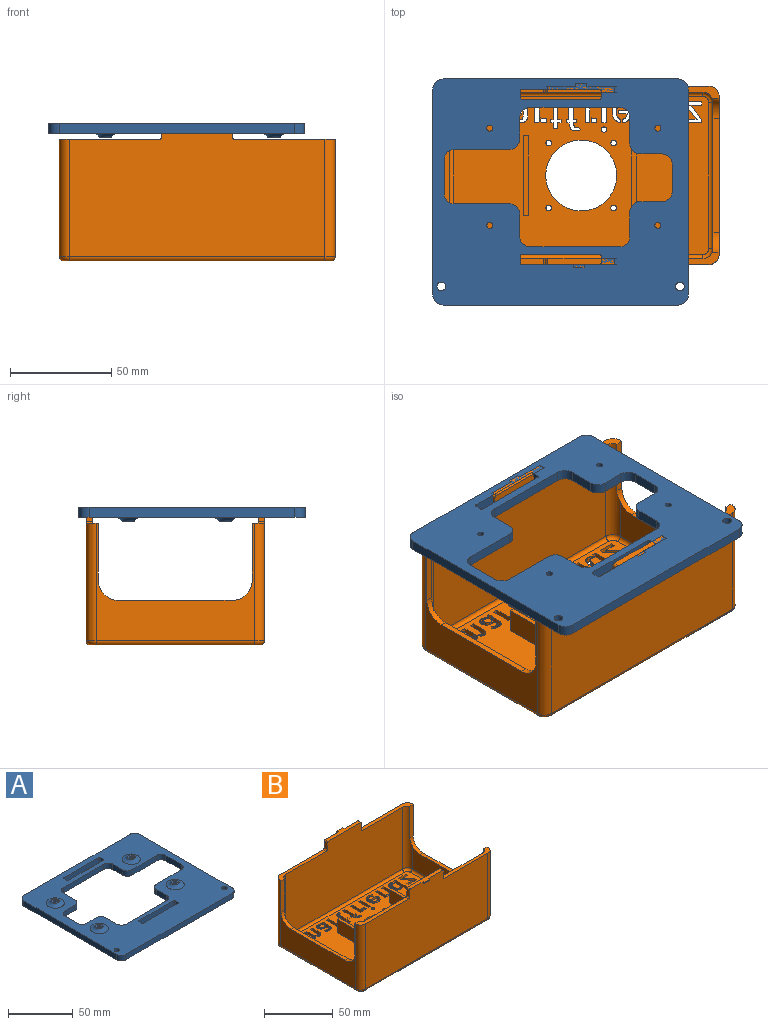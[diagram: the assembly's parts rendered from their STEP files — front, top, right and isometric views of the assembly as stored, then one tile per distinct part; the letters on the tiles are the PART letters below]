
ASSEMBLY  parts=2 mates=1
PART A: 64 faces, bbox 126x111.5x10 mm
  f0: plane 5x3mm, normal (-1,0,0), area 15mm2, adj f18,f19,f22,f27
  f1: plane 38x5mm, normal (0,1,0), area 190mm2, adj f18,f19,f22,f23
  f2: plane 5x3mm, normal (1,0,0), area 15mm2, adj f18,f19,f23,f26
  f3: plane 101.5x5mm, normal (1,0,0), area 507.5mm2, adj f18,f19,f28,f30
  f4: plane 116x5mm, normal (0,1,0), area 580mm2, adj f18,f19,f28,f29
  f5: plane 101.5x5mm, normal (-1,0,0), area 507.5mm2, adj f18,f19,f29,f31
  f6: plane 5x3mm, normal (1,0,0), area 15mm2, adj f18,f19,f20,f25
  f7: plane 38x5mm, normal (0,-1,0), area 190mm2, adj f18,f19,f20,f21
  f8: plane 5x3mm, normal (-1,0,0), area 15mm2, adj f18,f19,f21,f24
  f9: cylinder r=1.5mm len=7mm, axis (0,0,-1), area 66mm2, adj f19,f34
  f10: cylinder r=1.5mm len=7mm, axis (0,0,-1), area 66mm2, adj f19,f33
  f11: cylinder r=1.5mm len=7mm, axis (0,0,-1), area 66mm2, adj f19,f32
  f12: plane 38x5mm, normal (0,-1,0), area 190mm2, adj f18,f19,f26,f27
  f13: cylinder r=2.15mm len=5mm, axis (0,0,-1), area 67.5mm2, adj f18,f19
  f14: cylinder r=2.15mm len=5mm, axis (0,0,-1), area 67.5mm2, adj f18,f19
  f15: plane 116x5mm, normal (0,-1,0), area 580mm2, adj f18,f19,f30,f31
  f16: plane 38x5mm, normal (0,1,0), area 190mm2, adj f18,f19,f24,f25
  f17: cylinder r=1.5mm len=7mm, axis (0,0,-1), area 66mm2, adj f19,f35
  f18: plane 126x111.5mm, normal (0,0,1), area 7777mm2, adj f0,f1,f2,f3,f4,f5,f6,f7
  f19: plane 126x111.5mm, normal (0,0,-1), area 8364.4mm2, adj f0,f1,f2,f3,f4,f5,f6,f7
  f20: cylinder r=1mm len=5mm, axis (0,0,-1), area 7.9mm2, adj f6,f7,f18,f19
  f21: cylinder r=1mm len=5mm, axis (0,0,1), area 7.9mm2, adj f7,f8,f18,f19
  f22: cylinder r=1mm len=5mm, axis (0,0,1), area 7.9mm2, adj f0,f1,f18,f19
  f23: cylinder r=1mm len=5mm, axis (0,0,-1), area 7.9mm2, adj f1,f2,f18,f19
  f24: cylinder r=1mm len=5mm, axis (0,0,-1), area 7.9mm2, adj f8,f16,f18,f19
  f25: cylinder r=1mm len=5mm, axis (0,0,1), area 7.9mm2, adj f6,f16,f18,f19
  f26: cylinder r=1mm len=5mm, axis (0,0,1), area 7.9mm2, adj f2,f12,f18,f19
  f27: cylinder r=1mm len=5mm, axis (0,0,-1), area 7.9mm2, adj f0,f12,f18,f19
  f28: cylinder r=5mm len=5mm, axis (0,0,-1), area 39.3mm2, adj f3,f4,f18,f19
  f29: cylinder r=5mm len=5mm, axis (0,0,1), area 39.3mm2, adj f4,f5,f18,f19
  f30: cylinder r=5mm len=5mm, axis (0,0,1), area 39.3mm2, adj f3,f15,f18,f19
  f31: cylinder r=5mm len=5mm, axis (0,0,-1), area 39.3mm2, adj f5,f15,f18,f19
  f32: plane 6x6mm, normal (0,0,1), area 21.2mm2, adj f11,f39
  f33: plane 6x6mm, normal (0,0,1), area 21.2mm2, adj f10,f38
  f34: plane 6x6mm, normal (0,0,1), area 21.2mm2, adj f9,f37
  f35: plane 6x6mm, normal (0,0,1), area 21.2mm2, adj f17,f36
  f36: torus R=7mm, axis (0,0,1), area 141.1mm2, adj f18,f35
  f37: torus R=7mm, axis (0,0,1), area 141.1mm2, adj f18,f34
  f38: torus R=7mm, axis (0,0,1), area 141.1mm2, adj f18,f33
  f39: torus R=7mm, axis (0,0,1), area 141.1mm2, adj f18,f32
  f40: plane 10.92x5mm, normal (0,1,0), area 54.6mm2, adj f18,f19,f54,f55
  f41: plane 12.23x5mm, normal (1,0,0), area 61.2mm2, adj f18,f19,f55,f62
  f42: plane 44.32x5mm, normal (0,1,0), area 221.6mm2, adj f18,f19,f62,f63
  f43: plane 11.15x5mm, normal (-1,0,0), area 55.7mm2, adj f18,f19,f57,f63
  f44: plane 27.23x5mm, normal (0,1,0), area 136.2mm2, adj f18,f19,f57,f58
  f45: plane 16.9x5mm, normal (-1,0,0), area 84.5mm2, adj f18,f19,f58,f59
  f46: plane 27.23x5mm, normal (0,-1,0), area 136.2mm2, adj f18,f19,f56,f59
  f47: plane 10.72x5mm, normal (-1,0,0), area 53.6mm2, adj f18,f19,f56,f60
  f48: plane 44.32x5mm, normal (0,-1,0), area 221.6mm2, adj f18,f19,f60,f61
  f49: plane 13x5mm, normal (1,0,0), area 65mm2, adj f18,f19,f52,f61
  f50: plane 10.92x5mm, normal (0,-1,0), area 54.6mm2, adj f18,f19,f52,f53
  f51: plane 13.53x5mm, normal (1,0,0), area 67.7mm2, adj f18,f19,f53,f54
  f52: cylinder r=5mm len=5mm, axis (0,0,-1), area 39.3mm2, adj f18,f19,f49,f50
  f53: cylinder r=5mm len=5mm, axis (0,0,1), area 39.3mm2, adj f18,f19,f50,f51
  f54: cylinder r=5mm len=5mm, axis (0,0,-1), area 39.3mm2, adj f18,f19,f40,f51
  f55: cylinder r=5mm len=5mm, axis (0,0,1), area 39.3mm2, adj f18,f19,f40,f41
  f56: cylinder r=5mm len=5mm, axis (0,0,1), area 39.3mm2, adj f18,f19,f46,f47
  f57: cylinder r=5mm len=5mm, axis (0,0,-1), area 39.3mm2, adj f18,f19,f43,f44
  f58: cylinder r=5mm len=5mm, axis (0,0,1), area 39.3mm2, adj f18,f19,f44,f45
  f59: cylinder r=5mm len=5mm, axis (0,0,-1), area 39.3mm2, adj f18,f19,f45,f46
  f60: cylinder r=5mm len=5mm, axis (0,0,-1), area 39.3mm2, adj f18,f19,f47,f48
  f61: cylinder r=5mm len=5mm, axis (0,0,1), area 39.3mm2, adj f18,f19,f48,f49
  f62: cylinder r=5mm len=5mm, axis (0,0,-1), area 39.3mm2, adj f18,f19,f41,f42
  f63: cylinder r=5mm len=5mm, axis (0,0,1), area 39.3mm2, adj f18,f19,f42,f43
PART B: 408 faces, bbox 136.8x91x68 mm
  f0: plane 126x78mm, normal (0,0,1), area 8098mm2, adj f6,f7,f8,f9,f10,f59,f60,f61
  f1: plane 132x84mm, normal (0,0,-1), area 9558.3mm2, adj f6,f7,f8,f9,f10,f51,f52,f53
  f2: plane 49.5x6mm, normal (0,0,1), area 157.2mm2, adj f4,f14,f17,f28,f36,f43,f44
  f3: plane 49.5x6mm, normal (0,0,1), area 157.2mm2, adj f12,f15,f16,f19,f40,f47,f48
  f4: plane 78x58mm, normal (-1,0,0), area 1676.7mm2, adj f2,f5,f24,f25,f26,f27,f28,f44
  f5: plane 49.5x6mm, normal (0,0,1), area 157.2mm2, adj f4,f12,f15,f27,f39,f49,f50
  f6: cylinder r=1.4mm len=3mm, axis (0,0,-1), area 26.4mm2, adj f0,f1
  f7: cylinder r=1.4mm len=3mm, axis (0,0,-1), area 26.4mm2, adj f0,f1
  f8: cylinder r=1.4mm len=3mm, axis (0,0,-1), area 26.4mm2, adj f0,f1
  f9: cylinder r=1.4mm len=3mm, axis (0,0,-1), area 26.4mm2, adj f0,f1
  f10: cylinder r=17.5mm len=35mm, axis (0,0,-1), area 329.9mm2, adj f0,f1
  f11: plane 72x20.97mm, normal (1,0,0), area 1241.2mm2, adj f24,f25,f26,f43,f49,f62
  f12: plane 120x63mm, normal (0,1,0), area 6880mm2, adj f3,f5,f29,f30,f31,f39,f40,f41
  f13: plane 72x20.97mm, normal (-1,0,0), area 1241.2mm2, adj f20,f21,f23,f45,f48,f63
  f14: plane 120x63mm, normal (0,-1,0), area 6880mm2, adj f2,f18,f32,f33,f34,f35,f36,f37
  f15: plane 126x66mm, normal (0,-1,0), area 7579.7mm2, adj f3,f5,f29,f30,f31,f39,f40,f41
  f16: plane 78x58mm, normal (1,0,0), area 1676.7mm2, adj f3,f18,f19,f20,f21,f22,f23,f46
  f17: plane 126x66mm, normal (0,1,0), area 7577.5mm2, adj f2,f18,f32,f33,f34,f35,f36,f37
  f18: plane 49.5x6mm, normal (0,0,1), area 157.2mm2, adj f14,f16,f17,f22,f35,f45,f46
  f19: plane 28.03x3.42mm, normal (0,1,0), area 95.8mm2, adj f3,f16,f23,f48
  f20: plane 56x3mm, normal (0,0,1), area 168mm2, adj f13,f16,f21,f23
  f21: cylinder r=10mm len=10mm, axis (-1,0,0), area 48.5mm2, adj f13,f16,f20,f22,f45
  f22: plane 28.03x3.42mm, normal (0,-1,0), area 95.8mm2, adj f16,f18,f21,f45
  f23: cylinder r=10mm len=10mm, axis (-1,0,0), area 48.5mm2, adj f13,f16,f19,f20,f48
  f24: cylinder r=10mm len=10mm, axis (-1,0,0), area 48.5mm2, adj f4,f11,f26,f27,f49
  f25: cylinder r=10mm len=10mm, axis (-1,0,0), area 48.5mm2, adj f4,f11,f26,f28,f43
  f26: plane 56x3mm, normal (0,0,1), area 168mm2, adj f4,f11,f24,f25
  f27: plane 28.03x3.42mm, normal (0,1,0), area 95.8mm2, adj f4,f5,f24,f49
  f28: plane 28.03x3.42mm, normal (0,-1,0), area 95.8mm2, adj f2,f4,f25,f43
  f29: plane 6x3mm, normal (1,0,0), area 18mm2, adj f12,f15,f40,f42
  f30: plane 6x3mm, normal (-1,0,0), area 18mm2, adj f12,f15,f39,f41
  f31: plane 33x4.5mm, normal (0,0,1), area 106.8mm2, adj f12,f15,f41,f42,f67,f68,f70
  f32: plane 6x3mm, normal (-1,0,0), area 18mm2, adj f14,f17,f36,f38
  f33: plane 6x3mm, normal (1,0,0), area 18mm2, adj f14,f17,f35,f37
  f34: plane 33x4.5mm, normal (0,0,1), area 107.8mm2, adj f14,f17,f37,f38,f71,f72,f74
  f35: cylinder r=1mm len=3mm, axis (0,1,0), area 4.7mm2, adj f14,f17,f18,f33
  f36: cylinder r=1mm len=3mm, axis (0,-1,0), area 4.7mm2, adj f2,f14,f17,f32
  f37: cylinder r=1mm len=3mm, axis (0,-1,0), area 4.7mm2, adj f14,f17,f33,f34
  f38: cylinder r=1mm len=3mm, axis (0,1,0), area 4.7mm2, adj f14,f17,f32,f34
  f39: cylinder r=1mm len=3mm, axis (0,-1,0), area 4.7mm2, adj f5,f12,f15,f30
  f40: cylinder r=1mm len=3mm, axis (0,1,0), area 4.7mm2, adj f3,f12,f15,f29
  f41: cylinder r=1mm len=3mm, axis (0,1,0), area 4.7mm2, adj f12,f15,f30,f31
  f42: cylinder r=1mm len=3mm, axis (0,-1,0), area 4.7mm2, adj f12,f15,f29,f31
  f43: cylinder r=5mm len=55mm, axis (0,0,1), area 366mm2, adj f2,f11,f14,f25,f28,f60
  f44: cylinder r=5mm len=58mm, axis (0,0,-1), area 455.5mm2, adj f2,f4,f17,f56
  f45: cylinder r=5mm len=55mm, axis (0,0,-1), area 366mm2, adj f13,f14,f18,f21,f22,f61
  f46: cylinder r=5mm len=58mm, axis (0,0,1), area 455.5mm2, adj f16,f17,f18,f57
  f47: cylinder r=5mm len=58mm, axis (0,0,-1), area 455.5mm2, adj f3,f15,f16,f53
  f48: cylinder r=5mm len=55mm, axis (0,0,1), area 366mm2, adj f3,f12,f13,f19,f23,f65
  f49: cylinder r=5mm len=55mm, axis (0,0,-1), area 366mm2, adj f5,f11,f12,f24,f27,f64
  f50: cylinder r=5mm len=58mm, axis (0,0,1), area 455.5mm2, adj f4,f5,f15,f52
  f51: cylinder r=2mm len=126mm, axis (1,0,0), area 395.8mm2, adj f1,f15,f52,f53
  f52: torus R=3mm, axis (0,0,1), area 21.1mm2, adj f1,f50,f51,f54
  f53: torus R=3mm, axis (0,0,1), area 21.1mm2, adj f1,f47,f51,f55
  f54: cylinder r=2mm len=78mm, axis (0,-1,0), area 245mm2, adj f1,f4,f52,f56
  f55: cylinder r=2mm len=78mm, axis (0,1,0), area 245mm2, adj f1,f16,f53,f57
  f56: torus R=3mm, axis (0,0,1), area 21.1mm2, adj f1,f44,f54,f58
  f57: torus R=3mm, axis (0,0,1), area 21.1mm2, adj f1,f46,f55,f58
  f58: cylinder r=2mm len=126mm, axis (-1,0,0), area 395.8mm2, adj f1,f17,f56,f57
  f59: cylinder r=2mm len=120mm, axis (1,0,0), area 377mm2, adj f0,f14,f60,f61
  f60: torus R=3mm, axis (0,0,1), area 21.1mm2, adj f0,f43,f59,f62
  f61: torus R=3mm, axis (0,0,1), area 21.1mm2, adj f0,f45,f59,f63
  f62: cylinder r=2mm len=72mm, axis (0,1,0), area 226.2mm2, adj f0,f11,f60,f64
  f63: cylinder r=2mm len=72mm, axis (0,-1,0), area 226.2mm2, adj f0,f13,f61,f65
  f64: torus R=3mm, axis (0,0,1), area 21.1mm2, adj f0,f49,f62,f66
  f65: torus R=3mm, axis (0,0,1), area 21.1mm2, adj f0,f48,f63,f66
  f66: cylinder r=2mm len=120mm, axis (-1,0,0), area 377mm2, adj f0,f12,f64,f65
  f67: plane 1.6x1.5mm, normal (1,0,0), area 1.8mm2, adj f15,f31,f69,f70
  f68: plane 1.6x1.5mm, normal (-1,0,0), area 1.8mm2, adj f15,f31,f69,f70
  f69: plane 5.21x1.5mm, normal (0,-0.5,-0.87), area 9mm2, adj f15,f67,f68,f70
  f70: plane 5.21x0.73mm, normal (0,-1,0), area 3.8mm2, adj f31,f67,f68,f69
  f71: plane 1.8x1.5mm, normal (-1,0,0), area 2.1mm2, adj f17,f34,f73,f74
  f72: plane 1.8x1.5mm, normal (1,0,0), area 2.1mm2, adj f17,f34,f73,f74
  f73: plane 5.85x1.5mm, normal (0,0.5,-0.87), area 10.1mm2, adj f17,f71,f72,f74
  f74: plane 5.85x0.93mm, normal (0,1,0), area 5.5mm2, adj f34,f71,f72,f73
  f75: plane 3x1.54mm, normal (-0.9,-0.43,0), area 5.1mm2, adj f0,f1,f76,f80
  f76: extruded ~3x1.37mm, area 4.5mm2, adj f0,f1,f75,f77
  f77: extruded ~3x1.54mm, area 4.7mm2, adj f0,f1,f76,f78
  f78: plane 3x1.83mm, normal (1,0,0), area 5.5mm2, adj f0,f1,f77,f79
  f79: extruded ~3x1.12mm, area 3.4mm2, adj f0,f1,f78,f80
  f80: extruded ~3x1.07mm, area 3.4mm2, adj f0,f1,f75,f79
  f81: extruded ~3x1.32mm, area 4.1mm2, adj f0,f1,f82,f104
  f82: extruded ~3x0.92mm, area 3.5mm2, adj f0,f1,f81,f83
  f83: extruded ~3x1.07mm, area 3.6mm2, adj f0,f1,f82,f84
  f84: extruded ~3x1.34mm, area 4.1mm2, adj f0,f1,f83,f85
  f85: extruded ~3x0.98mm, area 3mm2, adj f0,f1,f84,f86
  f86: extruded ~3x1.12mm, area 3.5mm2, adj f0,f1,f85,f87
  f87: extruded ~3x0.97mm, area 3.6mm2, adj f0,f1,f86,f88
  f88: extruded ~3x1.13mm, area 3.8mm2, adj f0,f1,f87,f89
  f89: plane 3x1.78mm, normal (-1,0,0), area 5.3mm2, adj f0,f1,f88,f90
  f90: extruded ~3x1.69mm, area 5.3mm2, adj f0,f1,f89,f91
  f91: extruded ~3x1.38mm, area 5.4mm2, adj f0,f1,f90,f92
  f92: extruded ~3x1.66mm, area 5.7mm2, adj f0,f1,f91,f93
  f93: extruded ~3x2mm, area 6.1mm2, adj f0,f1,f92,f94
  f94: extruded ~3x2.07mm, area 6.4mm2, adj f0,f1,f93,f95
  f95: extruded ~3x1.69mm, area 5.9mm2, adj f0,f1,f94,f96
  f96: extruded ~3x1.52mm, area 5.7mm2, adj f0,f1,f95,f97
  f97: extruded ~3x1.91mm, area 5.9mm2, adj f0,f1,f96,f98
  f98: extruded ~3x2.07mm, area 6.4mm2, adj f0,f1,f97,f99
  f99: extruded ~3x1.43mm, area 5.5mm2, adj f0,f1,f98,f100
  f100: plane 3x1.24mm, normal (-0.84,0.55,0), area 4.5mm2, adj f0,f1,f99,f101
  f101: extruded ~3x0.6mm, area 2.3mm2, adj f0,f1,f100,f102
  f102: extruded ~3x0.69mm, area 2.3mm2, adj f0,f1,f101,f103
  f103: extruded ~3x0.65mm, area 2mm2, adj f0,f1,f102,f104
  f104: extruded ~3x0.51mm, area 1.5mm2, adj f0,f1,f81,f103
  f105: plane 3x2mm, normal (0,1,0), area 6mm2, adj f0,f1,f106,f109
  f106: plane 10.44x3mm, normal (1,0,0), area 31.3mm2, adj f0,f1,f105,f107
  f107: plane 3x2.24mm, normal (0,-1,0), area 6.7mm2, adj f0,f1,f106,f108
  f108: plane 9.39x3mm, normal (-1,0,0), area 28.2mm2, adj f0,f1,f107,f109
  f109: plane 3x1.05mm, normal (-0.98,0.22,0), area 3.2mm2, adj f0,f1,f105,f108
  f110: extruded ~3x1.15mm, area 4.4mm2, adj f0,f1,f111,f127
  f111: extruded ~3x1.41mm, area 4.4mm2, adj f0,f1,f110,f112
  f112: extruded ~3x1.14mm, area 3.5mm2, adj f0,f1,f111,f113
  f113: extruded ~3x1.08mm, area 3.5mm2, adj f0,f1,f112,f114
  f114: plane 3x1.43mm, normal (1,0,0), area 4.3mm2, adj f0,f1,f113,f115
  f115: extruded ~3x0.84mm, area 2.7mm2, adj f0,f1,f114,f116
  f116: extruded ~3x0.69mm, area 2.1mm2, adj f0,f1,f115,f117
  f117: extruded ~3x0.98mm, area 3.1mm2, adj f0,f1,f116,f118
  f118: extruded ~3x0.69mm, area 2.7mm2, adj f0,f1,f117,f119
  f119: extruded ~3x1.02mm, area 3.2mm2, adj f0,f1,f118,f120
  f120: extruded ~3x1.2mm, area 3.6mm2, adj f0,f1,f119,f121
  f121: plane 5.69x3mm, normal (1,0,0), area 17.1mm2, adj f0,f1,f120,f122
  f122: plane 3x2.26mm, normal (0,-1,0), area 6.8mm2, adj f0,f1,f121,f123
  f123: plane 5.87x3mm, normal (-1,0,0), area 17.6mm2, adj f0,f1,f122,f124
  f124: extruded ~3x0.91mm, area 2.7mm2, adj f0,f1,f123,f125
  f125: extruded ~3x0.92mm, area 2.8mm2, adj f0,f1,f124,f126
  f126: extruded ~3x0.87mm, area 2.7mm2, adj f0,f1,f125,f127
  f127: extruded ~3x0.73mm, area 2.7mm2, adj f0,f1,f110,f126
  f128: plane 3x2.26mm, normal (0,1,0), area 6.8mm2, adj f0,f1,f129,f132
  f129: plane 13.14x3mm, normal (1,0,0), area 39.4mm2, adj f0,f1,f128,f130
  f130: plane 3x1.24mm, normal (0.99,-0.1,0), area 3.7mm2, adj f0,f1,f129,f131
  f131: plane 3x2.13mm, normal (0,-1,0), area 6.4mm2, adj f0,f1,f130,f132
  f132: plane 14.39x3mm, normal (-1,0,0), area 43.2mm2, adj f0,f1,f128,f131
  f133: extruded ~3x2.34mm, area 7.1mm2, adj f0,f1,f134,f157
  f134: extruded ~3x1.97mm, area 6.7mm2, adj f0,f1,f133,f135
  f135: extruded ~3x1.27mm, area 4.7mm2, adj f0,f1,f134,f136
  f136: extruded ~3x1.45mm, area 4.5mm2, adj f0,f1,f135,f137
  f137: extruded ~3x1.23mm, area 3.7mm2, adj f0,f1,f136,f138
  f138: extruded ~3x1.03mm, area 3.3mm2, adj f0,f1,f137,f139
  f139: plane 3x1.93mm, normal (-1,0,0), area 5.8mm2, adj f0,f1,f138,f140
  f140: extruded ~3x1.53mm, area 5.3mm2, adj f0,f1,f139,f141
  f141: extruded ~3x0.99mm, area 3.1mm2, adj f0,f1,f140,f142
  f142: extruded ~3x0.77mm, area 3.3mm2, adj f0,f1,f141,f143
  f143: extruded ~3x1.12mm, area 3.7mm2, adj f0,f1,f142,f144
  f144: extruded ~3x1.38mm, area 4.2mm2, adj f0,f1,f143,f145
  f145: extruded ~3x1.39mm, area 4.2mm2, adj f0,f1,f144,f146
  f146: extruded ~3x1.15mm, area 3.7mm2, adj f0,f1,f145,f147
  f147: extruded ~3x0.79mm, area 3.3mm2, adj f0,f1,f146,f148
  f148: extruded ~3x1.02mm, area 3.2mm2, adj f0,f1,f147,f149
  f149: extruded ~3x0.87mm, area 2.7mm2, adj f0,f1,f148,f150
  f150: extruded ~3x0.7mm, area 2.7mm2, adj f0,f1,f149,f151
  f151: plane 3x1.96mm, normal (-1,0,0), area 5.9mm2, adj f0,f1,f150,f152
  f152: extruded ~3x0.92mm, area 3mm2, adj f0,f1,f151,f153
  f153: extruded ~3x1.09mm, area 3.3mm2, adj f0,f1,f152,f154
  f154: extruded ~3x1.51mm, area 4.6mm2, adj f0,f1,f153,f155
  f155: extruded ~3x1.4mm, area 5mm2, adj f0,f1,f154,f156
  f156: extruded ~3x1.59mm, area 5.7mm2, adj f0,f1,f155,f157
  f157: extruded ~3x2.42mm, area 7.4mm2, adj f0,f1,f133,f156
  f158: plane 3x1.8mm, normal (1,0,0), area 5.4mm2, adj f0,f1,f159,f169
  f159: plane 5.74x3mm, normal (0,-1,0), area 17.2mm2, adj f0,f1,f158,f160
  f160: plane 3x0.37mm, normal (0.62,0.78,0), area 1.4mm2, adj f0,f1,f159,f161
  f161: plane 6.56x5.37mm, normal (0.77,0.63,0), area 25.4mm2, adj f0,f1,f160,f162
  f162: plane 3x1.8mm, normal (1,0,0), area 5.4mm2, adj f0,f1,f161,f163
  f163: plane 7.94x3mm, normal (0,-1,0), area 23.8mm2, adj f0,f1,f162,f164
  f164: plane 3x1.8mm, normal (-1,0,0), area 5.4mm2, adj f0,f1,f163,f165
  f165: plane 5.74x3mm, normal (0,1,0), area 17.2mm2, adj f0,f1,f164,f166
  f166: plane 3x0.37mm, normal (-0.62,-0.78,0), area 1.4mm2, adj f0,f1,f165,f167
  f167: plane 6.56x5.37mm, normal (-0.77,-0.63,0), area 25.4mm2, adj f0,f1,f166,f168
  f168: plane 3x1.8mm, normal (-1,0,0), area 5.4mm2, adj f0,f1,f167,f169
  f169: plane 7.94x3mm, normal (0,1,0), area 23.8mm2, adj f0,f1,f158,f168
  f170: extruded ~3x1.52mm, area 4.9mm2, adj f0,f1,f171,f183
  f171: extruded ~3x1.47mm, area 5.5mm2, adj f0,f1,f170,f172
  f172: extruded ~3x0.64mm, area 2.1mm2, adj f0,f1,f171,f173
  f173: extruded ~3x0.64mm, area 2mm2, adj f0,f1,f172,f174
  f174: plane 3x1.98mm, normal (-1,0,0), area 5.9mm2, adj f0,f1,f173,f175
  f175: extruded ~3x0.73mm, area 2.6mm2, adj f0,f1,f174,f176
  f176: extruded ~3x0.71mm, area 2.4mm2, adj f0,f1,f175,f177
  f177: extruded ~3x0.83mm, area 2.7mm2, adj f0,f1,f176,f178
  f178: extruded ~3x0.75mm, area 2.6mm2, adj f0,f1,f177,f179
  f179: plane 3x1.85mm, normal (-1,0,0), area 5.6mm2, adj f0,f1,f178,f180
  f180: extruded ~3x1.21mm, area 3.7mm2, adj f0,f1,f179,f181
  f181: extruded ~3x1.05mm, area 3.7mm2, adj f0,f1,f180,f182
  f182: extruded ~3x0.96mm, area 3.6mm2, adj f0,f1,f181,f183
  f183: extruded ~3x1.27mm, area 3.9mm2, adj f0,f1,f170,f182
  f184: plane 3x1.89mm, normal (1,0,0), area 5.7mm2, adj f0,f1,f185,f190
  f185: extruded ~3x0.79mm, area 2.4mm2, adj f0,f1,f184,f186
  f186: extruded ~3x0.83mm, area 2.5mm2, adj f0,f1,f185,f187
  f187: extruded ~3x1.26mm, area 3.8mm2, adj f0,f1,f186,f188
  f188: plane 3x2.33mm, normal (-1,0,0), area 7mm2, adj f0,f1,f187,f189
  f189: extruded ~3x1.76mm, area 5.3mm2, adj f0,f1,f188,f190
  f190: extruded ~3x1.11mm, area 3.6mm2, adj f0,f1,f184,f189
  f191: plane 10.44x3mm, normal (-1,0,0), area 31.3mm2, adj f0,f1,f192,f194
  f192: plane 3x2.26mm, normal (0,1,0), area 6.8mm2, adj f0,f1,f191,f193
  f193: plane 10.44x3mm, normal (1,0,0), area 31.3mm2, adj f0,f1,f192,f194
  f194: plane 3x2.26mm, normal (0,-1,0), area 6.8mm2, adj f0,f1,f191,f193
  f195: extruded ~3x0.95mm, area 3.2mm2, adj f0,f1,f196,f202
  f196: extruded ~3x0.94mm, area 3.1mm2, adj f0,f1,f195,f197
  f197: extruded ~3x0.93mm, area 3.1mm2, adj f0,f1,f196,f198
  f198: extruded ~3x0.95mm, area 3.2mm2, adj f0,f1,f197,f199
  f199: extruded ~3x0.93mm, area 3.1mm2, adj f0,f1,f198,f200
  f200: extruded ~3x0.94mm, area 3.1mm2, adj f0,f1,f199,f201
  f201: extruded ~3x0.94mm, area 3.1mm2, adj f0,f1,f200,f202
  f202: extruded ~3x0.93mm, area 3.1mm2, adj f0,f1,f195,f201
  f203: plane 3x1.74mm, normal (1,0,0), area 5.2mm2, adj f0,f1,f204,f215
  f204: extruded ~3x0.91mm, area 2.9mm2, adj f0,f1,f203,f205
  f205: extruded ~3x0.71mm, area 2.9mm2, adj f0,f1,f204,f206
  f206: extruded ~3x0.82mm, area 2.8mm2, adj f0,f1,f205,f207
  f207: extruded ~3x0.93mm, area 2.8mm2, adj f0,f1,f206,f208
  f208: plane 4.28x3mm, normal (0,1,0), area 12.8mm2, adj f0,f1,f207,f209
  f209: plane 3x1.63mm, normal (1,0,0), area 4.9mm2, adj f0,f1,f208,f210
  f210: plane 6.35x3mm, normal (0,-1,0), area 19mm2, adj f0,f1,f209,f211
  f211: extruded ~3x0.89mm, area 2.7mm2, adj f0,f1,f210,f212
  f212: extruded ~3x1.89mm, area 5.8mm2, adj f0,f1,f211,f213
  f213: extruded ~3x1.61mm, area 5.5mm2, adj f0,f1,f212,f214
  f214: extruded ~3x1.38mm, area 5.4mm2, adj f0,f1,f213,f215
  f215: extruded ~3x1.81mm, area 5.7mm2, adj f0,f1,f203,f214
  f216: plane 3x2mm, normal (0,1,0), area 6mm2, adj f0,f1,f217,f220
  f217: plane 10.44x3mm, normal (1,0,0), area 31.3mm2, adj f0,f1,f216,f218
  f218: plane 3x2.24mm, normal (0,-1,0), area 6.7mm2, adj f0,f1,f217,f219
  f219: plane 9.37x3mm, normal (-1,0,0), area 28.1mm2, adj f0,f1,f218,f220
  f220: plane 3x1.07mm, normal (-0.98,0.22,0), area 3.3mm2, adj f0,f1,f216,f219
  f221: extruded ~3x0.51mm, area 1.5mm2, adj f0,f1,f222,f244
  f222: extruded ~3x0.62mm, area 2mm2, adj f0,f1,f221,f223
  f223: plane 3x1.33mm, normal (-0.88,-0.48,0), area 4.5mm2, adj f0,f1,f222,f224
  f224: extruded ~3x0.41mm, area 1.4mm2, adj f0,f1,f223,f225
  f225: extruded ~3x0.56mm, area 1.8mm2, adj f0,f1,f224,f226
  f226: extruded ~3x0.62mm, area 1.9mm2, adj f0,f1,f225,f227
  f227: extruded ~3x0.59mm, area 1.8mm2, adj f0,f1,f226,f228
  f228: extruded ~3x1.56mm, area 4.8mm2, adj f0,f1,f227,f229
  f229: extruded ~3x0.98mm, area 4mm2, adj f0,f1,f228,f230
  f230: extruded ~3x1.28mm, area 4.2mm2, adj f0,f1,f229,f231
  f231: extruded ~3x1.53mm, area 4.6mm2, adj f0,f1,f230,f232
  f232: plane 3x1.41mm, normal (0,1,0), area 4.2mm2, adj f0,f1,f231,f233
  f233: plane 3x1.52mm, normal (1,0,0), area 4.6mm2, adj f0,f1,f232,f234
  f234: plane 3x1.37mm, normal (0,-1,0), area 4.1mm2, adj f0,f1,f233,f235
  f235: plane 8.93x3mm, normal (1,0,0), area 26.8mm2, adj f0,f1,f234,f236
  f236: plane 3x2.26mm, normal (0,-1,0), area 6.8mm2, adj f0,f1,f235,f237
  f237: plane 8.93x3mm, normal (-1,0,0), area 26.8mm2, adj f0,f1,f236,f238
  f238: plane 3x1.65mm, normal (0,-1,0), area 4.9mm2, adj f0,f1,f237,f239
  f239: plane 3x1.52mm, normal (-1,0,0), area 4.6mm2, adj f0,f1,f238,f240
  f240: plane 3x1.61mm, normal (0,1,0), area 4.8mm2, adj f0,f1,f239,f241
  f241: extruded ~3x0.92mm, area 2.8mm2, adj f0,f1,f240,f242
  f242: extruded ~3x0.77mm, area 2.4mm2, adj f0,f1,f241,f243
  f243: extruded ~3x0.52mm, area 2mm2, adj f0,f1,f242,f244
  f244: extruded ~3x0.62mm, area 2mm2, adj f0,f1,f221,f243
  f245: plane 5.76x3mm, normal (-1,0,0), area 17.3mm2, adj f0,f1,f246,f269
  f246: plane 3x1.67mm, normal (0,-1,0), area 5mm2, adj f0,f1,f245,f247
  f247: plane 3x1.52mm, normal (-1,0,0), area 4.6mm2, adj f0,f1,f246,f248
  f248: plane 3x1.67mm, normal (0,1,0), area 5mm2, adj f0,f1,f247,f249
  f249: plane 3x2.96mm, normal (-1,0,0), area 8.9mm2, adj f0,f1,f248,f250
  f250: plane 3x2.24mm, normal (0,1,0), area 6.7mm2, adj f0,f1,f249,f251
  f251: plane 3x2.96mm, normal (1,0,0), area 8.9mm2, adj f0,f1,f250,f252
  f252: plane 3x1.37mm, normal (0,1,0), area 4.1mm2, adj f0,f1,f251,f253
  f253: plane 3x1.52mm, normal (1,0,0), area 4.6mm2, adj f0,f1,f252,f254
  f254: plane 3x1.37mm, normal (0,-1,0), area 4.1mm2, adj f0,f1,f253,f255
  f255: plane 5.63x3mm, normal (1,0,0), area 16.9mm2, adj f0,f1,f254,f256
  f256: extruded ~3x0.78mm, area 2.3mm2, adj f0,f1,f255,f257
  f257: extruded ~3x1.03mm, area 3.2mm2, adj f0,f1,f256,f258
  f258: extruded ~3x0.96mm, area 3.3mm2, adj f0,f1,f257,f259
  f259: extruded ~3x0.98mm, area 3.4mm2, adj f0,f1,f258,f260
  f260: extruded ~3x0.49mm, area 1.5mm2, adj f0,f1,f259,f261
  f261: extruded ~3x0.57mm, area 1.7mm2, adj f0,f1,f260,f262
  f262: extruded ~3x0.56mm, area 1.7mm2, adj f0,f1,f261,f263
  f263: extruded ~3x0.49mm, area 1.5mm2, adj f0,f1,f262,f264
  f264: extruded ~3x0.48mm, area 1.5mm2, adj f0,f1,f263,f265
  f265: plane 3x1.37mm, normal (-1,0,0), area 4.1mm2, adj f0,f1,f264,f266
  f266: extruded ~3x0.81mm, area 2.4mm2, adj f0,f1,f265,f267
  f267: extruded ~3x0.69mm, area 2.2mm2, adj f0,f1,f266,f268
  f268: extruded ~3x0.54mm, area 2.2mm2, adj f0,f1,f267,f269
  f269: extruded ~3x0.98mm, area 3mm2, adj f0,f1,f245,f268
  f270: plane 3x1.89mm, normal (1,0,0), area 5.7mm2, adj f0,f1,f271,f276
  f271: extruded ~3x0.79mm, area 2.4mm2, adj f0,f1,f270,f272
  f272: extruded ~3x0.83mm, area 2.5mm2, adj f0,f1,f271,f273
  f273: extruded ~3x1.26mm, area 3.8mm2, adj f0,f1,f272,f274
  f274: plane 3x2.33mm, normal (-1,0,0), area 7mm2, adj f0,f1,f273,f275
  f275: extruded ~3x1.76mm, area 5.3mm2, adj f0,f1,f274,f276
  f276: extruded ~3x1.11mm, area 3.6mm2, adj f0,f1,f270,f275
  f277: plane 3x1.5mm, normal (0.85,0.53,0), area 5.3mm2, adj f0,f1,f278,f285
  f278: extruded ~3x0.81mm, area 2.8mm2, adj f0,f1,f277,f279
  f279: extruded ~3x0.77mm, area 2.5mm2, adj f0,f1,f278,f280
  f280: extruded ~3x0.77mm, area 2.3mm2, adj f0,f1,f279,f281
  f281: extruded ~3x0.85mm, area 2.6mm2, adj f0,f1,f280,f282
  f282: plane 3x1.72mm, normal (-1,0,0), area 5.2mm2, adj f0,f1,f281,f283
  f283: plane 3x0.09mm, normal (0,1,0), area 0.3mm2, adj f0,f1,f282,f284
  f284: extruded ~3x1.29mm, area 3.9mm2, adj f0,f1,f283,f285
  f285: extruded ~3x0.88mm, area 3mm2, adj f0,f1,f277,f284
  f286: plane 3x1.96mm, normal (1,0,0), area 5.9mm2, adj f0,f1,f287,f299
  f287: extruded ~3x0.94mm, area 3.2mm2, adj f0,f1,f286,f288
  f288: extruded ~3x0.75mm, area 2.6mm2, adj f0,f1,f287,f289
  f289: extruded ~3x0.77mm, area 2.6mm2, adj f0,f1,f288,f290
  f290: extruded ~3x0.97mm, area 3.2mm2, adj f0,f1,f289,f291
  f291: plane 3x1.76mm, normal (1,0,0), area 5.3mm2, adj f0,f1,f290,f292
  f292: extruded ~3x1.28mm, area 4mm2, adj f0,f1,f291,f293
  f293: extruded ~3x1.03mm, area 3.6mm2, adj f0,f1,f292,f294
  f294: extruded ~3x0.93mm, area 3.5mm2, adj f0,f1,f293,f295
  f295: extruded ~3x1.26mm, area 3.9mm2, adj f0,f1,f294,f296
  f296: extruded ~3x1.23mm, area 3.9mm2, adj f0,f1,f295,f297
  f297: extruded ~3x0.82mm, area 3.4mm2, adj f0,f1,f296,f298
  f298: extruded ~3x1.05mm, area 3.6mm2, adj f0,f1,f297,f299
  f299: extruded ~3x1.13mm, area 3.6mm2, adj f0,f1,f286,f298
  f300: plane 3x2.02mm, normal (0,1,0), area 6.1mm2, adj f0,f1,f301,f304
  f301: plane 10.44x3mm, normal (1,0,0), area 31.3mm2, adj f0,f1,f300,f302
  f302: plane 3x2.26mm, normal (0,-1,0), area 6.8mm2, adj f0,f1,f301,f303
  f303: plane 9.37x3mm, normal (-1,0,0), area 28.1mm2, adj f0,f1,f302,f304
  f304: plane 3x1.07mm, normal (-0.98,0.22,0), area 3.3mm2, adj f0,f1,f300,f303
  f305: extruded ~3x0.96mm, area 2.9mm2, adj f0,f1,f306,f320
  f306: extruded ~3x1.02mm, area 3.4mm2, adj f0,f1,f305,f307
  f307: plane 3x1.46mm, normal (1,0,0), area 4.4mm2, adj f0,f1,f306,f308
  f308: extruded ~3x0.98mm, area 3.1mm2, adj f0,f1,f307,f309
  f309: extruded ~3x0.56mm, area 1.7mm2, adj f0,f1,f308,f310
  f310: extruded ~3x0.77mm, area 2.5mm2, adj f0,f1,f309,f311
  f311: extruded ~3x0.69mm, area 2.4mm2, adj f0,f1,f310,f312
  f312: extruded ~3x1.01mm, area 3.1mm2, adj f0,f1,f311,f313
  f313: extruded ~3x1.19mm, area 3.6mm2, adj f0,f1,f312,f314
  f314: plane 5.69x3mm, normal (1,0,0), area 17.1mm2, adj f0,f1,f313,f315
  f315: plane 3x2.22mm, normal (0,-1,0), area 6.7mm2, adj f0,f1,f314,f316
  f316: plane 7.11x3mm, normal (-1,0,0), area 21.3mm2, adj f0,f1,f315,f317
  f317: extruded ~3x1.38mm, area 4.2mm2, adj f0,f1,f316,f318
  f318: extruded ~3x1.1mm, area 3.9mm2, adj f0,f1,f317,f319
  f319: extruded ~3x0.97mm, area 3.6mm2, adj f0,f1,f318,f320
  f320: extruded ~3x1.18mm, area 3.7mm2, adj f0,f1,f305,f319
  f321: plane 3x2mm, normal (0,1,0), area 6mm2, adj f0,f1,f322,f325
  f322: plane 10.44x3mm, normal (1,0,0), area 31.3mm2, adj f0,f1,f321,f323
  f323: plane 3x2.24mm, normal (0,-1,0), area 6.7mm2, adj f0,f1,f322,f324
  f324: plane 9.37x3mm, normal (-1,0,0), area 28.1mm2, adj f0,f1,f323,f325
  f325: plane 3x1.07mm, normal (-0.98,0.22,0), area 3.3mm2, adj f0,f1,f321,f324
  f326: plane 3x2.55mm, normal (-1,0,0), area 7.7mm2, adj f0,f1,f327,f360
  f327: extruded ~3x1.31mm, area 3.9mm2, adj f0,f1,f326,f328
  f328: extruded ~3x1.31mm, area 4mm2, adj f0,f1,f327,f329
  f329: extruded ~3x1.08mm, area 3.5mm2, adj f0,f1,f328,f330
  f330: extruded ~3x0.76mm, area 3.1mm2, adj f0,f1,f329,f331
  f331: extruded ~3x0.96mm, area 3.1mm2, adj f0,f1,f330,f332
  f332: extruded ~3x1.08mm, area 3.3mm2, adj f0,f1,f331,f333
  f333: extruded ~3x1.18mm, area 3.5mm2, adj f0,f1,f332,f334
  f334: extruded ~3x1.05mm, area 3.2mm2, adj f0,f1,f333,f335
  f335: extruded ~3x0.85mm, area 2.8mm2, adj f0,f1,f334,f336
  f336: extruded ~3x0.55mm, area 2.1mm2, adj f0,f1,f335,f337
  f337: plane 3x1.28mm, normal (0.84,-0.55,0), area 4.6mm2, adj f0,f1,f336,f338
  f338: extruded ~3x0.34mm, area 1.3mm2, adj f0,f1,f337,f339
  f339: extruded ~3x0.54mm, area 1.9mm2, adj f0,f1,f338,f340
  f340: extruded ~3x0.67mm, area 2.1mm2, adj f0,f1,f339,f341
  f341: extruded ~3x0.77mm, area 2.3mm2, adj f0,f1,f340,f342
  f342: extruded ~3x0.77mm, area 2.3mm2, adj f0,f1,f341,f343
  f343: extruded ~3x0.55mm, area 1.9mm2, adj f0,f1,f342,f344
  f344: extruded ~3x0.79mm, area 2.6mm2, adj f0,f1,f343,f345
  f345: extruded ~3x1.44mm, area 4.3mm2, adj f0,f1,f344,f346
  f346: plane 3.91x3mm, normal (1,0,0), area 11.7mm2, adj f0,f1,f345,f347
  f347: extruded ~3x0.64mm, area 2.7mm2, adj f0,f1,f346,f348
  f348: extruded ~3x0.81mm, area 2.7mm2, adj f0,f1,f347,f349
  f349: plane 3x1.41mm, normal (1,0,0), area 4.2mm2, adj f0,f1,f348,f350
  f350: extruded ~3x1.21mm, area 4mm2, adj f0,f1,f349,f351
  f351: extruded ~3x0.82mm, area 3.4mm2, adj f0,f1,f350,f352
  f352: extruded ~3x0.55mm, area 1.8mm2, adj f0,f1,f351,f353
  f353: extruded ~3x0.45mm, area 1.9mm2, adj f0,f1,f352,f354
  f354: extruded ~3x0.52mm, area 1.8mm2, adj f0,f1,f353,f355
  f355: extruded ~3x0.51mm, area 1.6mm2, adj f0,f1,f354,f356
  f356: plane 3x1.24mm, normal (-0.9,-0.43,0), area 4.1mm2, adj f0,f1,f355,f357
  f357: extruded ~3x0.32mm, area 1.4mm2, adj f0,f1,f356,f358
  f358: extruded ~3x0.54mm, area 1.7mm2, adj f0,f1,f357,f359
  f359: extruded ~3x0.58mm, area 1.8mm2, adj f0,f1,f358,f360
  f360: extruded ~3x0.44mm, area 1.3mm2, adj f0,f1,f326,f359
  f361: extruded ~3x0.97mm, area 3mm2, adj f0,f1,f362,f379
  f362: extruded ~3x0.58mm, area 2.5mm2, adj f0,f1,f361,f363
  f363: extruded ~3x0.76mm, area 2.4mm2, adj f0,f1,f362,f364
  f364: extruded ~3x0.78mm, area 2.3mm2, adj f0,f1,f363,f365
  f365: plane 3x0.41mm, normal (0,-1,0), area 1.2mm2, adj f0,f1,f364,f366
  f366: plane 3x1.32mm, normal (-1,0,0), area 3.9mm2, adj f0,f1,f365,f367
  f367: plane 3x0.81mm, normal (0,1,0), area 2.4mm2, adj f0,f1,f366,f368
  f368: extruded ~3x1.46mm, area 4.4mm2, adj f0,f1,f367,f369
  f369: extruded ~3x1.29mm, area 4.3mm2, adj f0,f1,f368,f370
  f370: extruded ~3x1.02mm, area 4.2mm2, adj f0,f1,f369,f371
  f371: extruded ~3x1.47mm, area 4.6mm2, adj f0,f1,f370,f372
  f372: extruded ~3x1.5mm, area 4.6mm2, adj f0,f1,f371,f373
  f373: extruded ~3x0.98mm, area 3.6mm2, adj f0,f1,f372,f374
  f374: extruded ~3x1.03mm, area 3.5mm2, adj f0,f1,f373,f375
  f375: extruded ~3x1.21mm, area 3.7mm2, adj f0,f1,f374,f376
  f376: extruded ~3x0.24mm, area 0.7mm2, adj f0,f1,f375,f377
  f377: plane 3x1.5mm, normal (-1,0,0), area 4.5mm2, adj f0,f1,f376,f378
  f378: extruded ~3x0.99mm, area 3.4mm2, adj f0,f1,f377,f379
  f379: extruded ~3x1.24mm, area 3.9mm2, adj f0,f1,f361,f378
  f380: extruded ~3x1.14mm, area 4.7mm2, adj f0,f1,f381,f397
  f381: extruded ~3x1.43mm, area 4.5mm2, adj f0,f1,f380,f382
  f382: extruded ~3x1.01mm, area 3.1mm2, adj f0,f1,f381,f383
  f383: extruded ~3x0.95mm, area 3.1mm2, adj f0,f1,f382,f384
  f384: plane 3x1.46mm, normal (1,0,0), area 4.4mm2, adj f0,f1,f383,f385
  f385: extruded ~3x0.86mm, area 2.7mm2, adj f0,f1,f384,f386
  f386: extruded ~3x0.66mm, area 2mm2, adj f0,f1,f385,f387
  f387: extruded ~3x0.76mm, area 2.5mm2, adj f0,f1,f386,f388
  f388: extruded ~3x0.69mm, area 2.4mm2, adj f0,f1,f387,f389
  f389: extruded ~3x1.01mm, area 3.1mm2, adj f0,f1,f388,f390
  f390: plane 3x1.19mm, normal (1,0,0), area 3.6mm2, adj f0,f1,f389,f391
  f391: plane 5.69x3mm, normal (1,0,0), area 17.1mm2, adj f0,f1,f390,f392
  f392: plane 3x2.24mm, normal (0,-1,0), area 6.7mm2, adj f0,f1,f391,f393
  f393: plane 5.87x3mm, normal (-1,0,0), area 17.6mm2, adj f0,f1,f392,f394
  f394: extruded ~3x0.92mm, area 2.8mm2, adj f0,f1,f393,f395
  f395: extruded ~3x0.84mm, area 2.5mm2, adj f0,f1,f394,f396
  f396: extruded ~3x0.79mm, area 2.4mm2, adj f0,f1,f395,f397
  f397: extruded ~3x0.71mm, area 2.4mm2, adj f0,f1,f380,f396
  f398: plane 39.28x12mm, normal (-1,0,0), area 471.3mm2, adj f0,f399,f401,f402
  f399: plane 12x2.52mm, normal (0,-1,0), area 30.3mm2, adj f0,f398,f400,f402
  f400: plane 39.28x12mm, normal (1,0,0), area 471.3mm2, adj f0,f399,f401,f402
  f401: plane 12x2.52mm, normal (0,1,0), area 30.3mm2, adj f0,f398,f400,f402
  f402: plane 39.28x2.52mm, normal (0,0,1), area 99.1mm2, adj f398,f399,f400,f401
  f403: plane 39.28x12mm, normal (-1,0,0), area 471.3mm2, adj f0,f404,f406,f407
  f404: plane 12x2.58mm, normal (0,-1,0), area 30.9mm2, adj f0,f403,f405,f407
  f405: plane 39.28x12mm, normal (1,0,0), area 471.3mm2, adj f0,f404,f406,f407
  f406: plane 12x2.58mm, normal (0,1,0), area 30.9mm2, adj f0,f403,f405,f407
  f407: plane 39.28x2.58mm, normal (0,0,1), area 101.2mm2, adj f403,f404,f405,f406
PLACE A rot(axis=(0,1,0),180deg) t=(87.47,27.8,99.47)mm
PLACE B t=(79.76,43.8,31.47)mm
MATE fastened A.f19 <-> B.f31  axis (0,0,1) through (74.22,47.8,99.47)mm
